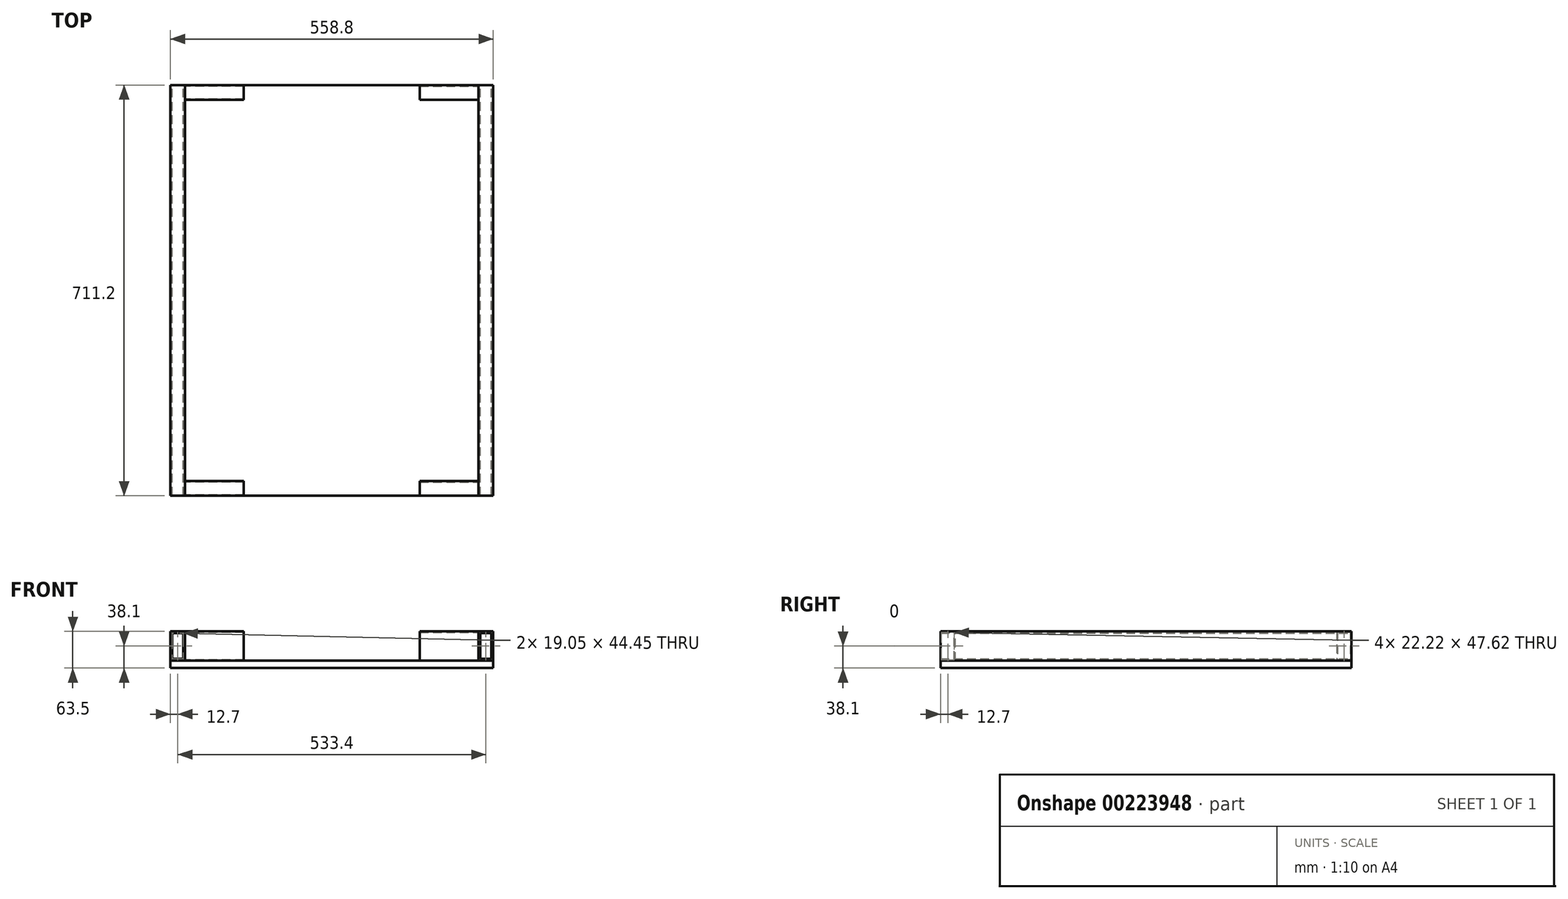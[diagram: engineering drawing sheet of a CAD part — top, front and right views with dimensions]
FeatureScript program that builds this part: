
annotation { "Feature Type Name" : "Feature", "Feature Type Description" : "" }
export const myFeature = defineFeature(function(context is Context, id is Id, definition is map)
    precondition{}
    {
        {
            var Q0;
            Q0=qCreatedBy(makeId("Front.planeOp"),FACE);
            var sketch = newSketch(context, id + "F0", { "sketchPlane" : qUnion([Q0])});
            skLineSegment(sketch, "E0.bottom", {"start": v(-254, 25.4) * mm, "end": v(-279.4, 25.4) * mm});
            skLineSegment(sketch, "E0.top", {"start": v(-254, -25.4) * mm, "end": v(-279.4, -25.4) * mm});
            skLineSegment(sketch, "E0.left", {"start": v(-254, 25.4) * mm, "end": v(-254, -25.4) * mm});
            skLineSegment(sketch, "E0.right", {"start": v(-279.4, 25.4) * mm, "end": v(-279.4, -25.4) * mm});
            skPoint(sketch, "E0.middle", {"position": v(-266.7, 0) * mm});
            skLineSegment(sketch, "E1.bottom", {"start": v(279.4, 25.4) * mm, "end": v(254, 25.4) * mm});
            skLineSegment(sketch, "E1.top", {"start": v(279.4, -25.4) * mm, "end": v(254, -25.4) * mm});
            skLineSegment(sketch, "E1.left", {"start": v(279.4, 25.4) * mm, "end": v(279.4, -25.4) * mm});
            skLineSegment(sketch, "E1.right", {"start": v(254, 25.4) * mm, "end": v(254, -25.4) * mm});
            skPoint(sketch, "E1.middle", {"position": v(266.7, 0) * mm});
            skLineSegment(sketch, "E2", {"start": v(-266.7, 0) * mm, "end": v(266.7, 0) * mm, "construction": true});
            skLineSegment(sketch, "E3.0", {"start": v(-257.18, 22.22) * mm, "end": v(-276.23, 22.22) * mm});
            skLineSegment(sketch, "E3.1", {"start": v(-257.18, 22.22) * mm, "end": v(-257.18, -22.23) * mm});
            skLineSegment(sketch, "E3.2", {"start": v(-257.18, -22.23) * mm, "end": v(-276.23, -22.23) * mm});
            skLineSegment(sketch, "E3.3", {"start": v(-276.23, 22.22) * mm, "end": v(-276.23, -22.23) * mm});
            skLineSegment(sketch, "E4.bottom", {"start": v(276.23, 22.22) * mm, "end": v(257.18, 22.22) * mm});
            skLineSegment(sketch, "E4.top", {"start": v(276.23, -22.23) * mm, "end": v(257.18, -22.23) * mm});
            skLineSegment(sketch, "E4.left", {"start": v(276.23, 22.22) * mm, "end": v(276.23, -22.23) * mm});
            skLineSegment(sketch, "E4.right", {"start": v(257.18, 22.22) * mm, "end": v(257.18, -22.23) * mm});
            skSolve(sketch);
        }
        {
            var Q0;
            Q0 = qSketchRegion(id + "F0", true);
            extrude(context, id + "F1", {"entities" : qUnion([Q0]), "depth" : 355.6 * mm, "hasSecondDirection" : true, "secondDirectionOppositeDirection" : true, "secondDirectionDepth" : 355.6 * mm});
        }
        {
            var Q0;
            Q0=makeQuery(id+"F1.opExtrude","SWEPT_FACE",FACE,{"disambiguationData":[OSD([sQuery(id+"F0.wireOp",EDGE,"E0.top")])]});
            var sketch = newSketch(context, id + "F2", { "sketchPlane" : qUnion([Q0])});
            skLineSegment(sketch, "E5.bottom", {"start": v(-279.4, -355.6) * mm, "end": v(279.4, -355.6) * mm});
            skLineSegment(sketch, "E5.top", {"start": v(-279.4, 355.6) * mm, "end": v(279.4, 355.6) * mm});
            skLineSegment(sketch, "E5.left", {"start": v(-279.4, -355.6) * mm, "end": v(-279.4, 355.6) * mm});
            skLineSegment(sketch, "E5.right", {"start": v(279.4, -355.6) * mm, "end": v(279.4, 355.6) * mm});
            skPoint(sketch, "E5.middle", {"position": v(0, 0) * mm});
            skSolve(sketch);
        }
        {
            var Q0;
            Q0 = qSketchRegion(id + "F2", true);
            extrude(context, id + "F3", {"entities" : qUnion([Q0]), "depth" : 12.7 * mm});
        }
        {
            var Q0;
            Q0=makeQuery(id+"F1.opExtrude","SWEPT_FACE",FACE,{"disambiguationData":[OSD([sQuery(id+"F0.wireOp",EDGE,"E1.right")])]});
            var sketch = newSketch(context, id + "F4", { "sketchPlane" : qUnion([Q0])});
            skLineSegment(sketch, "E6.bottom", {"start": v(-355.6, -25.4) * mm, "end": v(-330.2, -25.4) * mm});
            skLineSegment(sketch, "E6.top", {"start": v(-355.6, 25.4) * mm, "end": v(-330.2, 25.4) * mm});
            skLineSegment(sketch, "E6.left", {"start": v(-355.6, -25.4) * mm, "end": v(-355.6, 25.4) * mm});
            skLineSegment(sketch, "E6.right", {"start": v(-330.2, -25.4) * mm, "end": v(-330.2, 25.4) * mm});
            skLineSegment(sketch, "E7.bottom", {"start": v(355.6, -25.4) * mm, "end": v(330.2, -25.4) * mm});
            skLineSegment(sketch, "E7.top", {"start": v(355.6, 25.4) * mm, "end": v(330.2, 25.4) * mm});
            skLineSegment(sketch, "E7.left", {"start": v(355.6, -25.4) * mm, "end": v(355.6, 25.4) * mm});
            skLineSegment(sketch, "E7.right", {"start": v(330.2, -25.4) * mm, "end": v(330.2, 25.4) * mm});
            skLineSegment(sketch, "E8.0", {"start": v(-331.79, -23.81) * mm, "end": v(-331.79, 23.81) * mm});
            skLineSegment(sketch, "E8.1", {"start": v(-354.01, -23.81) * mm, "end": v(-331.79, -23.81) * mm});
            skLineSegment(sketch, "E8.2", {"start": v(-354.01, -23.81) * mm, "end": v(-354.01, 23.81) * mm});
            skLineSegment(sketch, "E8.3", {"start": v(-354.01, 23.81) * mm, "end": v(-331.79, 23.81) * mm});
            skLineSegment(sketch, "E9.0", {"start": v(331.79, -23.81) * mm, "end": v(331.79, 23.81) * mm});
            skLineSegment(sketch, "E9.1", {"start": v(354.01, -23.81) * mm, "end": v(331.79, -23.81) * mm});
            skLineSegment(sketch, "E9.2", {"start": v(354.01, -23.81) * mm, "end": v(354.01, 23.81) * mm});
            skLineSegment(sketch, "E9.3", {"start": v(354.01, 23.81) * mm, "end": v(331.79, 23.81) * mm});
            skSolve(sketch);
        }
        {
            var Q0;
            Q0 = qSketchRegion(id + "F4", true);
            var Q1;
            Q1=makeQuery(id+"F1.opExtrude","SWEPT_FACE",FACE,{"disambiguationData":[OSD([sQuery(id+"F0.wireOp",EDGE,"E0.left")])]});
            extrude(context, id + "F5", {"entities" : qUnion([Q0]), "endBoundEntityFace" : qUnion([Q1]), "depth" : 101.6 * mm});
        }
        {
            var Q0;
            Q0=makeQuery(id+"F1.opExtrude","SWEPT_FACE",FACE,{"disambiguationData":[OSD([sQuery(id+"F0.wireOp",EDGE,"E0.left")])]});
            var sketch = newSketch(context, id + "F6", { "sketchPlane" : qUnion([Q0])});
            skLineSegment(sketch, "E10.bottom", {"start": v(-355.6, 25.4) * mm, "end": v(-330.2, 25.4) * mm});
            skLineSegment(sketch, "E10.top", {"start": v(-355.6, -25.4) * mm, "end": v(-330.2, -25.4) * mm});
            skLineSegment(sketch, "E10.left", {"start": v(-355.6, 25.4) * mm, "end": v(-355.6, -25.4) * mm});
            skLineSegment(sketch, "E10.right", {"start": v(-330.2, 25.4) * mm, "end": v(-330.2, -25.4) * mm});
            skLineSegment(sketch, "E11.bottom", {"start": v(355.6, 25.4) * mm, "end": v(330.2, 25.4) * mm});
            skLineSegment(sketch, "E11.top", {"start": v(355.6, -25.4) * mm, "end": v(330.2, -25.4) * mm});
            skLineSegment(sketch, "E11.left", {"start": v(355.6, 25.4) * mm, "end": v(355.6, -25.4) * mm});
            skLineSegment(sketch, "E11.right", {"start": v(330.2, 25.4) * mm, "end": v(330.2, -25.4) * mm});
            skLineSegment(sketch, "E12.0", {"start": v(-354.01, 23.81) * mm, "end": v(-331.79, 23.81) * mm});
            skLineSegment(sketch, "E12.1", {"start": v(-354.01, 23.81) * mm, "end": v(-354.01, -23.81) * mm});
            skLineSegment(sketch, "E12.2", {"start": v(-354.01, -23.81) * mm, "end": v(-331.79, -23.81) * mm});
            skLineSegment(sketch, "E12.3", {"start": v(-331.79, 23.81) * mm, "end": v(-331.79, -23.81) * mm});
            skLineSegment(sketch, "E13.0", {"start": v(354.01, 23.81) * mm, "end": v(331.79, 23.81) * mm});
            skLineSegment(sketch, "E13.1", {"start": v(354.01, 23.81) * mm, "end": v(354.01, -23.81) * mm});
            skLineSegment(sketch, "E13.2", {"start": v(354.01, -23.81) * mm, "end": v(331.79, -23.81) * mm});
            skLineSegment(sketch, "E13.3", {"start": v(331.79, 23.81) * mm, "end": v(331.79, -23.81) * mm});
            skSolve(sketch);
        }
        {
            var Q0;
            Q0 = qSketchRegion(id + "F6", true);
            extrude(context, id + "F7", {"entities" : qUnion([Q0]), "depth" : 101.6 * mm});
        }
    });
